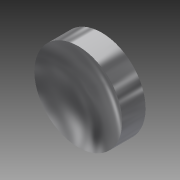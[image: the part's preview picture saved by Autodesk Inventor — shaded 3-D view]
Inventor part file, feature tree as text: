
AUTODESK INVENTOR PART (.ipt)
format: ipt  version: 2013 (Build 170138000, 138)  size: 116,224 bytes
history: native  units: in
note: dims shown in document units (in); Inventor stores cm internally (conversion verified against a paired STEP export)
features: revolve x1, sketch x1
ambient origin geometry x8: Origin, YZ Plane, XZ Plane, XY Plane, X Axis, Y Axis, Z Axis, Center Point
bodies: Solid1 (feature_tree)
feature tree (2):
  revolve  "Revolution1"  Angle=90.0deg
  sketch  "Sketch1"  dims[d0=0.025in d1=90.0deg d2=0.0935in d3=0.05in d4=90.0deg]
